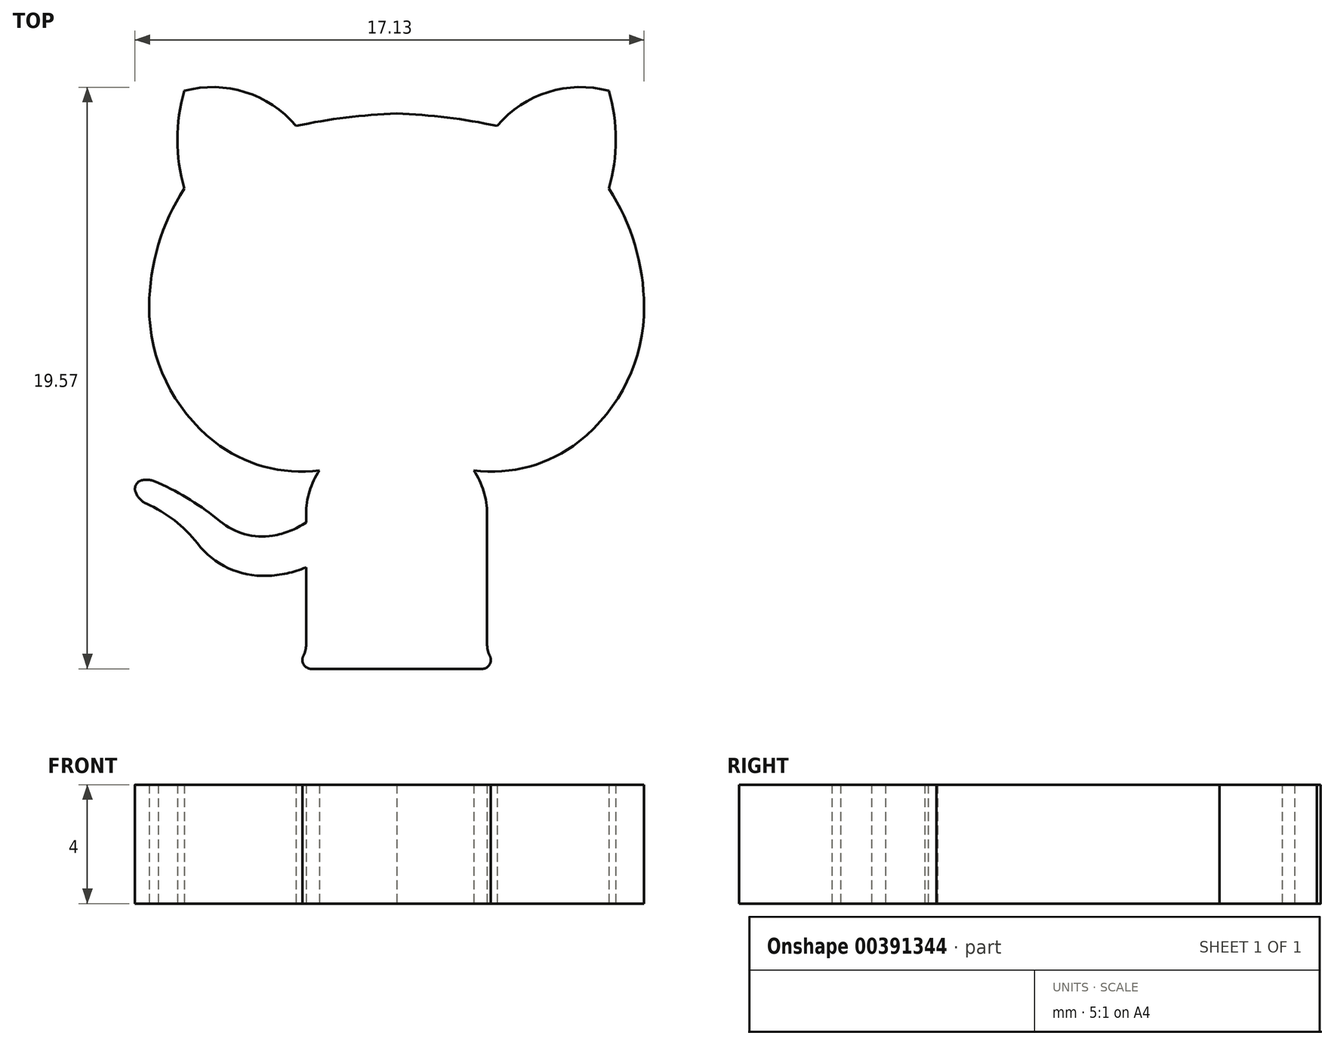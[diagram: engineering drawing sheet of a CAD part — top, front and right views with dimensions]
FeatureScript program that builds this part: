
annotation { "Feature Type Name" : "Feature", "Feature Type Description" : "" }
export const myFeature = defineFeature(function(context is Context, id is Id, definition is map)
    precondition{}
    {
        {
            var Q0;
            Q0=qCreatedBy(makeId("Top.planeOp"),FACE);
            var sketch = newSketch(context, id + "F0", { "sketchPlane" : qUnion([Q0])});
            skLineSegment(sketch, "E0", {"start": v(9.26, 11.92) * mm, "end": v(13.12, 11.92) * mm});
            skLineSegment(sketch, "E1", {"start": v(12.3, 12.73) * mm, "end": v(12.3, 17.13) * mm});
            skArc(sketch, "E2", {"start": v(12.3, 17.13) * mm, "mid": v(12.2, 17.9) * mm, "end": v(11.86, 18.6) * mm});
            skArc(sketch, "E3", {"start": v(11.86, 18.6) * mm, "mid": v(13.73, 18.72) * mm, "end": v(15.4, 19.57) * mm});
            skArc(sketch, "E4", {"start": v(15.4, 19.57) * mm, "mid": v(17.02, 21.59) * mm, "end": v(17.6, 24.12) * mm});
            skArc(sketch, "E5", {"start": v(17.6, 24.12) * mm, "mid": v(17.28, 26.18) * mm, "end": v(16.41, 28.08) * mm});
            skArc(sketch, "E6", {"start": v(16.41, 28.08) * mm, "mid": v(16.64, 29.72) * mm, "end": v(16.41, 31.37) * mm});
            skArc(sketch, "E7", {"start": v(16.41, 31.37) * mm, "mid": v(14.36, 31.32) * mm, "end": v(12.65, 30.19) * mm});
            skArc(sketch, "E8", {"start": v(12.65, 30.19) * mm, "mid": v(10.96, 30.47) * mm, "end": v(9.26, 30.6) * mm});
            skLineSegment(sketch, "E9", {"start": v(9.26, 30.6) * mm, "end": v(9.26, 11.92) * mm, "construction": true});
            skArc(sketch, "E10", {"start": v(12.3, 12.73) * mm, "mid": v(12.55, 12.15) * mm, "end": v(13.12, 11.92) * mm});
            skLineSegment(sketch, "E11", {"start": v(9.26, 30.6) * mm, "end": v(20.29, 30.19) * mm, "construction": true});
            skArc(sketch, "E12.MirrorCS", {"start": v(3.13, 19.57) * mm, "mid": v(1.5, 21.59) * mm, "end": v(0.94, 24.12) * mm});
            skArc(sketch, "E13.MirrorCS", {"start": v(0.94, 24.12) * mm, "mid": v(1.24, 26.18) * mm, "end": v(2.12, 28.08) * mm});
            skArc(sketch, "E14.MirrorCS", {"start": v(6.22, 17.13) * mm, "mid": v(6.33, 17.9) * mm, "end": v(6.67, 18.6) * mm});
            skArc(sketch, "E15.MirrorCS", {"start": v(6.22, 12.73) * mm, "mid": v(5.98, 12.15) * mm, "end": v(5.4, 11.92) * mm});
            skLineSegment(sketch, "E16.MirrorCS", {"start": v(9.26, 11.92) * mm, "end": v(5.4, 11.92) * mm});
            skArc(sketch, "E17.MirrorCS", {"start": v(2.12, 31.37) * mm, "mid": v(4.17, 31.32) * mm, "end": v(5.88, 30.19) * mm});
            skArc(sketch, "E18.MirrorCS", {"start": v(5.88, 30.19) * mm, "mid": v(7.56, 30.47) * mm, "end": v(9.26, 30.6) * mm});
            skArc(sketch, "E19.MirrorCS", {"start": v(2.12, 28.08) * mm, "mid": v(1.89, 29.72) * mm, "end": v(2.12, 31.37) * mm});
            skArc(sketch, "E20.MirrorCS", {"start": v(6.67, 18.6) * mm, "mid": v(4.8, 18.72) * mm, "end": v(3.13, 19.57) * mm});
            skLineSegment(sketch, "E21.MirrorCS", {"start": v(6.22, 12.73) * mm, "end": v(6.22, 17.13) * mm});
            skSolve(sketch);
        }
        {
            var Q0;
            Q0 = qSketchRegion(id + "F0", true);
            extrude(context, id + "F1", {"entities" : qUnion([Q0]), "depth" : 4 * mm});
        }
        {
            var Q0;
            Q0=qCreatedBy(makeId("Top.planeOp"),FACE);
            var sketch = newSketch(context, id + "F2", { "sketchPlane" : qUnion([Q0])});
            skArc(sketch, "E22", {"start": v(5.1, 16.4) * mm, "mid": v(5.68, 16.56) * mm, "end": v(6.22, 16.84) * mm});
            skArc(sketch, "E23", {"start": v(3.32, 16.89) * mm, "mid": v(4.15, 16.45) * mm, "end": v(5.1, 16.4) * mm});
            skArc(sketch, "E24", {"start": v(3.32, 16.89) * mm, "mid": v(2.33, 17.6) * mm, "end": v(1.25, 18.17) * mm});
            skArc(sketch, "E25", {"start": v(1.25, 18.17) * mm, "mid": v(0.84, 18.28) * mm, "end": v(0.44, 18.17) * mm});
            skArc(sketch, "E26", {"start": v(0.44, 18.17) * mm, "mid": v(0.53, 17.76) * mm, "end": v(0.84, 17.47) * mm});
            skArc(sketch, "E27", {"start": v(2.56, 16.14) * mm, "mid": v(1.79, 16.91) * mm, "end": v(0.84, 17.47) * mm});
            skArc(sketch, "E28", {"start": v(2.56, 16.14) * mm, "mid": v(3.6, 15.31) * mm, "end": v(4.9, 15.05) * mm});
            skArc(sketch, "E29", {"start": v(4.9, 15.05) * mm, "mid": v(5.57, 15.13) * mm, "end": v(6.22, 15.33) * mm});
            skLineSegment(sketch, "E30", {"start": v(6.22, 16.84) * mm, "end": v(6.22, 15.33) * mm});
            skSolve(sketch);
        }
        {
            var Q0;
            Q0 = qSketchRegion(id + "F2", true);
            var Q1;
            Q1=makeQuery(id+"F1.opExtrude","CAP_FACE",FACE,{"disambiguationData":[OSD([sQuery(id+"F0.wireOp",EDGE,"E0"),sQuery(id+"F0.wireOp",EDGE,"E1"),sQuery(id+"F0.wireOp",EDGE,"E2"),sQuery(id+"F0.wireOp",EDGE,"E3"),sQuery(id+"F0.wireOp",EDGE,"E4"),sQuery(id+"F0.wireOp",EDGE,"E5"),sQuery(id+"F0.wireOp",EDGE,"E6"),sQuery(id+"F0.wireOp",EDGE,"E7"),sQuery(id+"F0.wireOp",EDGE,"E8"),sQuery(id+"F0.wireOp",EDGE,"E10"),sQuery(id+"F0.wireOp",EDGE,"E12.MirrorCS"),sQuery(id+"F0.wireOp",EDGE,"E13.MirrorCS"),sQuery(id+"F0.wireOp",EDGE,"E14.MirrorCS"),sQuery(id+"F0.wireOp",EDGE,"E15.MirrorCS"),sQuery(id+"F0.wireOp",EDGE,"E16.MirrorCS"),sQuery(id+"F0.wireOp",EDGE,"E17.MirrorCS"),sQuery(id+"F0.wireOp",EDGE,"E18.MirrorCS"),sQuery(id+"F0.wireOp",EDGE,"E19.MirrorCS"),sQuery(id+"F0.wireOp",EDGE,"E20.MirrorCS"),sQuery(id+"F0.wireOp",EDGE,"E21.MirrorCS")])],"isStart":false});
            extrude(context, id + "F3", {"entities" : qUnion([Q0]), "operationType" : NewBodyOperationType.ADD, "endBound" : BoundingType.UP_TO_SURFACE, "endBoundEntityFace" : qUnion([Q1]), "depth" : 25 * mm});
        }
        {
            var Q0;
            Q0=makeQuery(id+"F1.opExtrude","SWEPT_EDGE",EDGE,{"disambiguationData":[OSD([sQuery(id+"F0.wireOp",EDGE,"E0"),sQuery(id+"F0.wireOp",EDGE,"E10")])]});
            var Q1;
            Q1=makeQuery(id+"F1.opExtrude","SWEPT_EDGE",EDGE,{"disambiguationData":[OSD([sQuery(id+"F0.wireOp",EDGE,"E15.MirrorCS"),sQuery(id+"F0.wireOp",EDGE,"E16.MirrorCS")])]});
            var Q2;
            Q2=makeQuery(id+"F3.opExtrude","SWEPT_EDGE",EDGE,{"disambiguationData":[OSD([sQuery(id+"F2.wireOp",EDGE,"E25"),sQuery(id+"F2.wireOp",EDGE,"E26")])]});
            fillet(context, id + "F4", {"entities" : qUnion([Q0, Q1, Q2]), "radius" : 0.3 * mm, "tangentPropagation" : true, "allowEdgeOverflow" : false});
        }
    });
